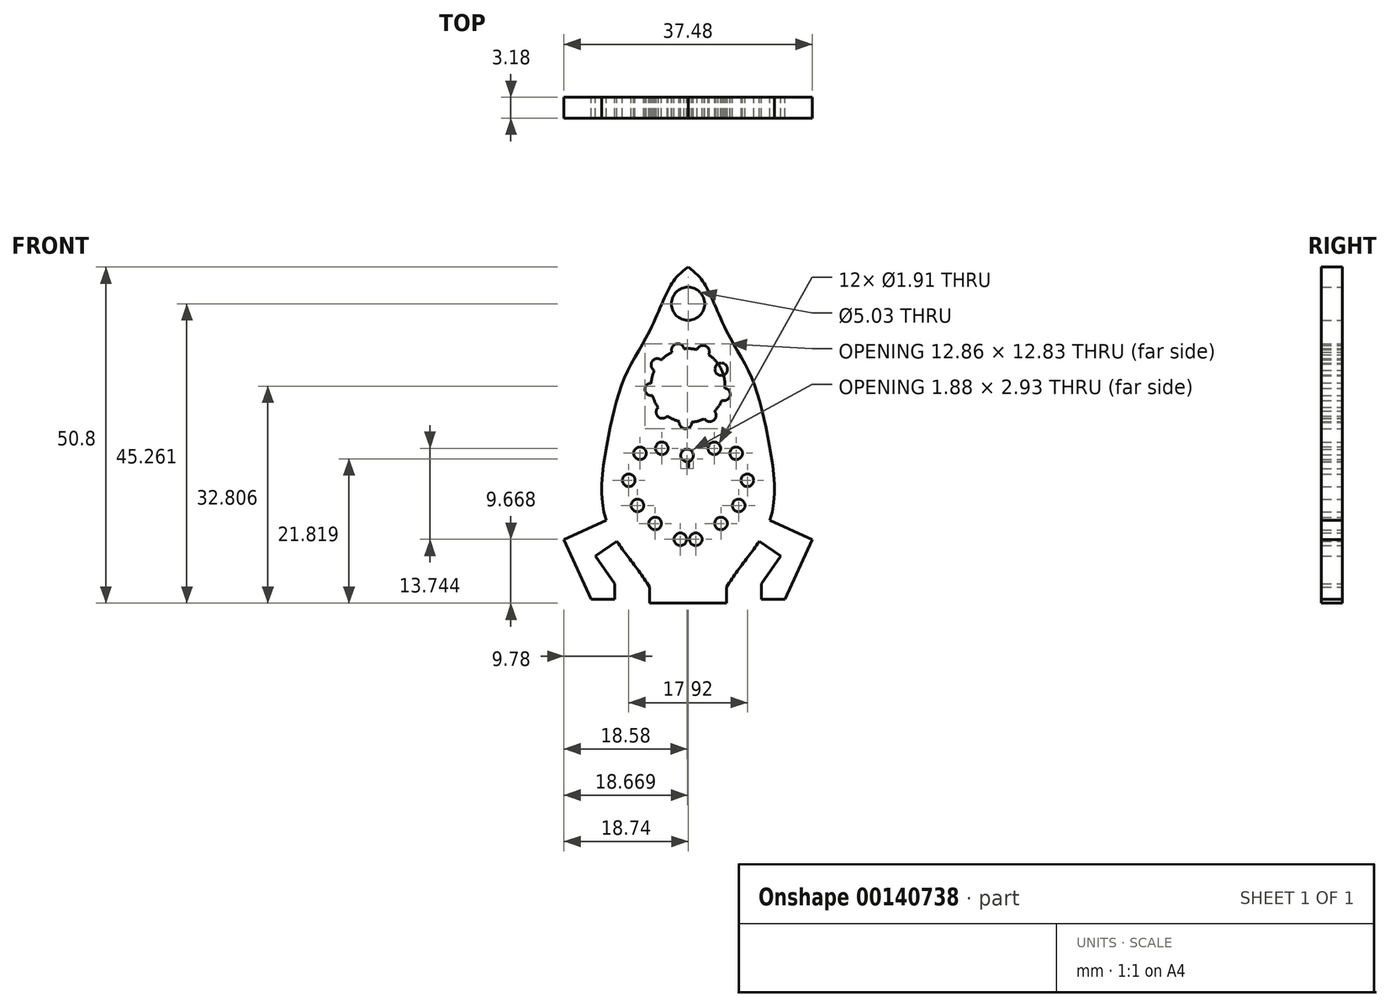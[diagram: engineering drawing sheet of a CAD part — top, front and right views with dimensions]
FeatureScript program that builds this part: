
annotation { "Feature Type Name" : "Feature", "Feature Type Description" : "" }
export const myFeature = defineFeature(function(context is Context, id is Id, definition is map)
    precondition{}
    {
        {
            var Q0;
            Q0=qCreatedBy(makeId("Front.planeOp"),FACE);
            var sketch = newSketch(context, id + "F0", { "sketchPlane" : qUnion([Q0])});
            skFitSpline(sketch, "E0", {"points": [v(-5.83, 20.12) * mm, v(5.83, 20.12) * mm], "startDerivative": vector(11.44, 0) * mm, "endDerivative": vector(11.44, 0) * mm});
            skFitSpline(sketch, "E1", {"points": [v(-5.83, 20.12) * mm, v(-9.5, 13.28) * mm, v(-12.22, 3.25) * mm, v(-12.36, -8.47) * mm, v(-5.83, -18.58) * mm], "startDerivative": vector(-15.95, -32) * mm, "endDerivative": vector(22.94, -39.8) * mm});
            skFitSpline(sketch, "E2", {"points": [v(5.83, 20.12) * mm, v(9.5, 13.28) * mm, v(12.22, 3.25) * mm, v(12.36, -8.47) * mm, v(5.83, -18.58) * mm], "startDerivative": vector(15.95, -32) * mm, "endDerivative": vector(-22.94, -39.8) * mm});
            skFitSpline(sketch, "E3", {"points": [v(-5.83, -18.58) * mm, v(5.83, -18.58) * mm], "startDerivative": vector(10.15, 0) * mm, "endDerivative": vector(10.15, 0) * mm});
            skLineSegment(sketch, "E4.bottom", {"start": v(-5.83, -18.58) * mm, "end": v(5.83, -18.58) * mm});
            skLineSegment(sketch, "E4.left", {"start": v(-5.83, -18.58) * mm, "end": v(-5.83, -21) * mm});
            skLineSegment(sketch, "E4.right", {"start": v(5.83, -18.58) * mm, "end": v(5.83, -21) * mm});
            skCircle(sketch, "E5", {"center": v(0, 11.91) * mm, "radius": 5.58 * mm});
            skFitSpline(sketch, "E6", {"points": [v(-5.83, 20.12) * mm, v(0, 29.8) * mm], "startDerivative": vector(8.06, 16.16) * mm, "endDerivative": vector(9.83, 6.94) * mm});
            skFitSpline(sketch, "E7", {"points": [v(0, 29.8) * mm, v(5.83, 20.12) * mm], "startDerivative": vector(9.83, -6.94) * mm, "endDerivative": vector(8.06, -16.16) * mm});
            skLineSegment(sketch, "E8", {"start": v(-12.36, -8.47) * mm, "end": v(-18.74, -11.37) * mm});
            skLineSegment(sketch, "E9", {"start": v(-18.74, -11.37) * mm, "end": v(-14.63, -20.42) * mm});
            skLineSegment(sketch, "E10", {"start": v(-11.1, -20.42) * mm, "end": v(-11.1, -18.06) * mm});
            skLineSegment(sketch, "E11", {"start": v(-11.1, -18.06) * mm, "end": v(-13.97, -13.86) * mm});
            skLineSegment(sketch, "E12", {"start": v(-13.97, -13.86) * mm, "end": v(-10.73, -11.65) * mm});
            skLineSegment(sketch, "E13.MirrorCS", {"start": v(11.1, -18.06) * mm, "end": v(13.97, -13.86) * mm});
            skLineSegment(sketch, "E14.MirrorCS", {"start": v(13.97, -13.86) * mm, "end": v(10.73, -11.65) * mm});
            skLineSegment(sketch, "E15.MirrorCS", {"start": v(11.1, -20.42) * mm, "end": v(11.1, -18.06) * mm});
            skLineSegment(sketch, "E16.MirrorCS", {"start": v(12.36, -8.47) * mm, "end": v(18.74, -11.37) * mm});
            skLineSegment(sketch, "E17.MirrorCS", {"start": v(18.74, -11.37) * mm, "end": v(14.63, -20.42) * mm});
            skCircle(sketch, "E18", {"center": v(0, 24.26) * mm, "radius": 2.51 * mm});
            skFitSpline(sketch, "E19", {"points": [v(0, -0.65) * mm, v(0.18, 1.4) * mm, v(4.38, 2.4) * mm, v(7.64, 1.4) * mm, v(8.99, -1.22) * mm, v(8.05, -5.34) * mm], "startDerivative": vector(4.9, 9.54) * mm, "endDerivative": vector(-8.13, -17.88) * mm});
            skFitSpline(sketch, "E20", {"points": [v(8.05, -5.34) * mm, v(6.76, -7.26) * mm, v(3.38, -10.25) * mm, v(0, -11.52) * mm], "startDerivative": vector(-5.72, -13.8) * mm, "endDerivative": vector(-10.73, -0.74) * mm});
            skCircle(sketch, "E21", {"center": v(-0.38, 6.34) * mm, "radius": 0.95 * mm});
            skCircle(sketch, "E22", {"center": v(1.16, -11.33) * mm, "radius": 0.95 * mm});
            skCircle(sketch, "E23", {"center": v(4.97, -8.94) * mm, "radius": 0.95 * mm});
            skCircle(sketch, "E24", {"center": v(7.64, -6.22) * mm, "radius": 0.95 * mm});
            skCircle(sketch, "E25", {"center": v(8.96, -2.41) * mm, "radius": 0.95 * mm});
            skCircle(sketch, "E26", {"center": v(7.26, 1.67) * mm, "radius": 0.95 * mm});
            skCircle(sketch, "E27", {"center": v(3.97, 2.41) * mm, "radius": 0.95 * mm});
            skCircle(sketch, "E28.MirrorC", {"center": v(-7.26, 1.67) * mm, "radius": 0.95 * mm});
            skCircle(sketch, "E29.MirrorC", {"center": v(-7.64, -6.22) * mm, "radius": 0.95 * mm});
            skCircle(sketch, "E30.MirrorC", {"center": v(-0.16, 1.35) * mm, "radius": 0.95 * mm});
            skCircle(sketch, "E31.MirrorC", {"center": v(-1.16, -11.33) * mm, "radius": 0.95 * mm});
            skCircle(sketch, "E32.MirrorC", {"center": v(-8.96, -2.41) * mm, "radius": 0.95 * mm});
            skCircle(sketch, "E33.MirrorC", {"center": v(-4.97, -8.94) * mm, "radius": 0.95 * mm});
            skFitSpline(sketch, "E34.MirrorCS", {"points": [v(-8.05, -5.34) * mm, v(-6.76, -7.26) * mm, v(-3.38, -10.25) * mm, v(0, -11.52) * mm], "startDerivative": vector(5.72, -13.8) * mm, "endDerivative": vector(10.73, -0.74) * mm});
            skFitSpline(sketch, "E35.MirrorCS", {"points": [v(0, -0.65) * mm, v(-0.18, 1.4) * mm, v(-4.38, 2.4) * mm, v(-7.64, 1.4) * mm, v(-8.99, -1.22) * mm, v(-8.05, -5.34) * mm], "startDerivative": vector(-4.9, 9.54) * mm, "endDerivative": vector(8.13, -17.88) * mm});
            skCircle(sketch, "E36.MirrorC", {"center": v(-3.97, 2.41) * mm, "radius": 0.95 * mm});
            skCircle(sketch, "E37.1.0", {"center": v(-3.87, 7.9) * mm, "radius": 0.95 * mm});
            skCircle(sketch, "E37.2.0", {"center": v(-5.55, 11.32) * mm, "radius": 0.95 * mm});
            skLineSegment(sketch, "E37.anchor1", {"start": v(0, 11.91) * mm, "end": v(-0.38, 6.34) * mm, "construction": true});
            skLineSegment(sketch, "E37.anchor2", {"start": v(0, 11.91) * mm, "end": v(-0.38, 6.34) * mm, "construction": true});
            skCircle(sketch, "E38.1.3.0", {"center": v(-4.63, 15.03) * mm, "radius": 0.95 * mm});
            skCircle(sketch, "E38.1.4.0", {"center": v(-1.55, 17.28) * mm, "radius": 0.95 * mm});
            skCircle(sketch, "E38.1.5.0", {"center": v(2.26, 17.01) * mm, "radius": 0.95 * mm});
            skCircle(sketch, "E38.1.6.0", {"center": v(5.01, 14.36) * mm, "radius": 0.95 * mm});
            skCircle(sketch, "E38.1.7.0", {"center": v(5.42, 10.57) * mm, "radius": 0.95 * mm});
            skCircle(sketch, "E39.1.8.0", {"center": v(3.29, 7.4) * mm, "radius": 0.95 * mm});
            skLineSegment(sketch, "E40", {"start": v(11.1, -20.42) * mm, "end": v(14.63, -20.42) * mm});
            skLineSegment(sketch, "E41", {"start": v(5.83, -21) * mm, "end": v(-5.83, -21) * mm});
            skLineSegment(sketch, "E42", {"start": v(-11.1, -20.42) * mm, "end": v(-14.63, -20.42) * mm});
            skSolve(sketch);
        }
        {
            var Q0;
            Q0 = qSketchRegion(id + "F0", true);
            var Q1;
            {var subQ0=sQuery(id+"F0.wireOp",EDGE,"E38.1.6.0");var subQ1=sQuery(id+"F0.wireOp",EDGE,"E5");var subQ18=makeQuery(id+"F0.imprint","INTERSECT",VERTEX,{"disambiguationData":[OD(0.0)],"derivedFrom":[subQ1,subQ0]});Q1=makeQuery(id+"F0.imprint","IMPRINT",FACE,{"disambiguationData":[TD([[makeQuery(id+"F0.imprint","IMPRINT",EDGE,{"disambiguationData":[TD([[subQ18,-1.0]])],"derivedFrom":subQ1}),1.0]])]});}
            var Q2;
            {var subQ4=sQuery(id+"F0.wireOp",EDGE,"E35.MirrorCS");var subQ9=sQuery(id+"F0.wireOp",EDGE,"E19");var subQ43=makeQuery(id+"F0.imprint","INTERSECT",VERTEX,{"derivedFrom":[subQ9,subQ4]});Q2=makeQuery(id+"F0.imprint","IMPRINT",FACE,{"disambiguationData":[TD([[makeQuery(id+"F0.imprint","IMPRINT",EDGE,{"disambiguationData":[TD([[subQ43,-1.0]])],"derivedFrom":subQ9}),-1.0]])]});}
            extrude(context, id + "F1", {"entities" : qUnion([Q0, Q1, Q2]), "depth" : 3.17 * mm});
        }
    });
